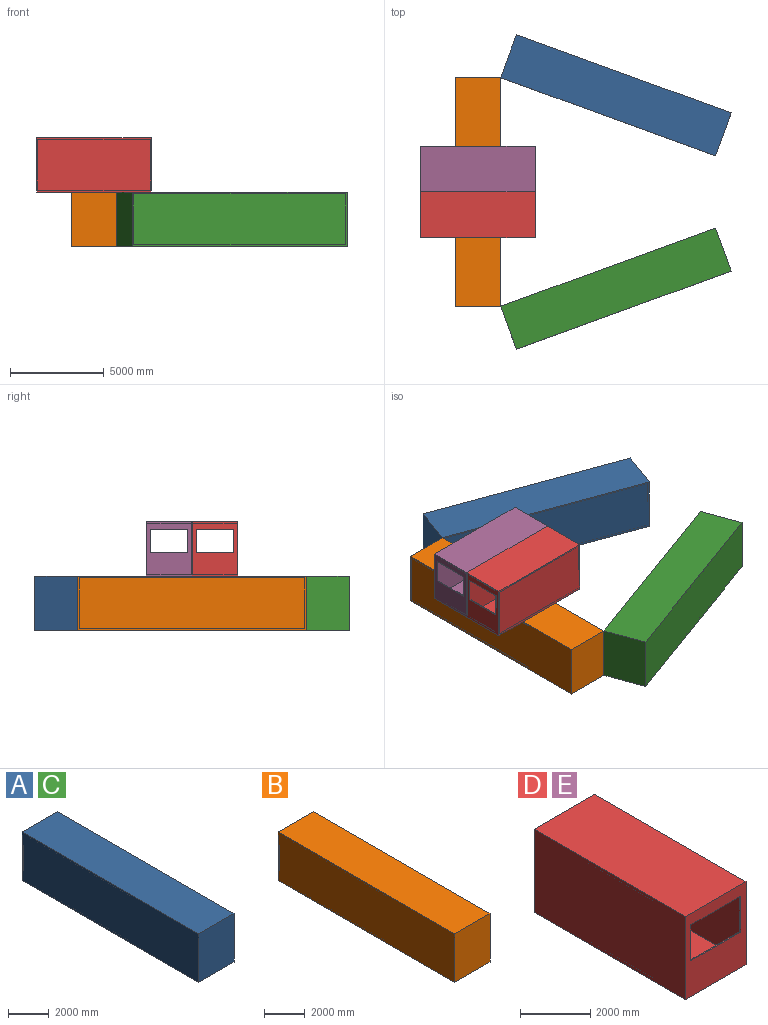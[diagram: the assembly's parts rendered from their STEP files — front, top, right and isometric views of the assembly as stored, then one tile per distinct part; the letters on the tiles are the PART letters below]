
ASSEMBLY  parts=5 mates=4
PART A: 12 faces, bbox 2438.4x12192x2896 mm
  f0: plane 2896x2438.4mm, normal (0,1,0), area 7061606.4mm2, adj f1,f3,f4,f5
  f1: plane 12192x2896mm, normal (-1,0,0), area 35308032mm2, adj f0,f2,f4,f5
  f2: plane 2896x2438.4mm, normal (0,-1,0), area 7061606.4mm2, adj f1,f3,f4,f5
  f3: plane 12192x2896mm, normal (1,0,0), area 35308032mm2, adj f0,f2,f4,f5
  f4: plane 12192x2438.4mm, normal (0,0,1), area 29728972.8mm2, adj f0,f1,f2,f3
  f5: plane 12192x2438.4mm, normal (0,0,-1), area 29728972.8mm2, adj f0,f1,f2,f3
  f6: plane 2697x2350mm, normal (0,-1,0), area 6337950mm2, adj f7,f9,f10,f11
  f7: plane 12024x2697mm, normal (1,0,0), area 32428728mm2, adj f6,f8,f10,f11
  f8: plane 2697x2350mm, normal (0,1,0), area 6337950mm2, adj f7,f9,f10,f11
  f9: plane 12024x2697mm, normal (-1,0,0), area 32428728mm2, adj f6,f8,f10,f11
  f10: plane 12024x2350mm, normal (0,0,1), area 28256400mm2, adj f6,f7,f8,f9
  f11: plane 12024x2350mm, normal (0,0,-1), area 28256400mm2, adj f6,f7,f8,f9
PART B: 16 faces, bbox 2438.4x12192x2896 mm
  f0: plane 12024x2697mm, normal (-1,0,0), area 16324728mm2, adj f1,f3,f4,f5,f6,f7,f8,f9
  f1: plane 2697x2350mm, normal (0,-1,0), area 6337950mm2, adj f0,f2,f4,f5
  f2: plane 12024x2697mm, normal (1,0,0), area 32428728mm2, adj f1,f3,f4,f5
  f3: plane 2697x2350mm, normal (0,1,0), area 6337950mm2, adj f0,f2,f4,f5
  f4: plane 12024x2350mm, normal (0,0,1), area 28256400mm2, adj f0,f1,f2,f3
  f5: plane 12024x2350mm, normal (0,0,-1), area 28256400mm2, adj f0,f1,f2,f3
  f6: plane 6000x44.2mm, normal (0,0,-1), area 265200mm2, adj f0,f7,f9,f10
  f7: plane 2684x44.2mm, normal (0,1,0), area 118632.8mm2, adj f0,f6,f8,f10
  f8: plane 6000x44.2mm, normal (0,0,1), area 265200mm2, adj f0,f7,f9,f10
  f9: plane 2684x44.2mm, normal (0,-1,0), area 118632.8mm2, adj f0,f6,f8,f10
  f10: plane 12192x2896mm, normal (1,0,0), area 19204032mm2, adj f6,f7,f8,f9,f11,f13,f14,f15
  f11: plane 2896x2438.4mm, normal (0,1,0), area 7061606.4mm2, adj f10,f12,f14,f15
  f12: plane 12192x2896mm, normal (-1,0,0), area 35308032mm2, adj f11,f13,f14,f15
  f13: plane 2896x2438.4mm, normal (0,-1,0), area 7061606.4mm2, adj f10,f12,f14,f15
  f14: plane 12192x2438.4mm, normal (0,0,1), area 29728972.8mm2, adj f10,f11,f12,f13
  f15: plane 12192x2438.4mm, normal (0,0,-1), area 29728972.8mm2, adj f10,f11,f12,f13
PART C: same geometry as A
PART D: 20 faces, bbox 2438.4x6096x2896 mm
  f0: plane 2692.4x2387.6mm, normal (0,-1,0), area 3928374.2mm2, adj f2,f3,f4,f5,f10,f11,f12,f13
  f1: plane 2692.4x2387.6mm, normal (0,1,0), area 3928374.2mm2, adj f2,f3,f4,f5,f6,f7,f8,f9
  f2: plane 6019.8x2692.4mm, normal (1,0,0), area 16207709.5mm2, adj f0,f1,f4,f5
  f3: plane 6019.8x2692.4mm, normal (-1,0,0), area 16207709.5mm2, adj f0,f1,f4,f5
  f4: plane 6019.8x2387.6mm, normal (0,0,1), area 14372874.5mm2, adj f0,f1,f2,f3
  f5: plane 6019.8x2387.6mm, normal (0,0,-1), area 14372874.5mm2, adj f0,f1,f2,f3
  f6: plane 2000x38.1mm, normal (0,0,-1), area 76200mm2, adj f1,f7,f9,f15
  f7: plane 1250x38.1mm, normal (-1,0,0), area 47625mm2, adj f1,f6,f8,f15
  f8: plane 2000x38.1mm, normal (0,0,1), area 76200mm2, adj f1,f7,f9,f15
  f9: plane 1250x38.1mm, normal (1,0,0), area 47625mm2, adj f1,f6,f8,f15
  f10: plane 1250x38.1mm, normal (1,0,0), area 47625mm2, adj f0,f11,f13,f14
  f11: plane 2000x38.1mm, normal (0,0,1), area 76200mm2, adj f0,f10,f12,f14
  f12: plane 1250x38.1mm, normal (-1,0,0), area 47625mm2, adj f0,f11,f13,f14
  f13: plane 2000x38.1mm, normal (0,0,-1), area 76200mm2, adj f0,f10,f12,f14
  f14: plane 2896x2438.4mm, normal (0,1,0), area 4561606.4mm2, adj f10,f11,f12,f13,f16,f17,f18,f19
  f15: plane 2896x2438.4mm, normal (0,-1,0), area 4561606.4mm2, adj f6,f7,f8,f9,f16,f17,f18,f19
  f16: plane 6096x2896mm, normal (-1,0,0), area 17654016mm2, adj f14,f15,f18,f19
  f17: plane 6096x2896mm, normal (1,0,0), area 17654016mm2, adj f14,f15,f18,f19
  f18: plane 6096x2438.4mm, normal (0,0,1), area 14864486.4mm2, adj f14,f15,f16,f17
  f19: plane 6096x2438.4mm, normal (0,0,-1), area 14864486.4mm2, adj f14,f15,f16,f17
PART E: same geometry as D
PLACE A rot(axis=(0,0,-1),110deg) t=(7364.56,5156.72,0)mm
PLACE B at identity fixed
PLACE C rot(axis=(0,0,-1),70deg) t=(7364.56,-5156.72,0)mm
PLACE D rot(axis=(0,0,-1),90deg) t=(0,-1219.2,2896)mm
PLACE E rot(axis=(0,0,-1),90deg) t=(0,1219.2,2896)mm
MATE revolute B.f14 <-> A.f4  axis (0,0,-1) through (1219.2,6096,1448)mm
MATE revolute C.f4 <-> B.f14  axis (0,0,1) through (1219.2,-6096,1448)mm
MATE fastened B.f14 <-> E.f19  axis (0,0,1) through (0,0,1448)mm
MATE fastened D.f19 <-> B.f14  axis (0,0,-1) through (0,0,1448)mm
